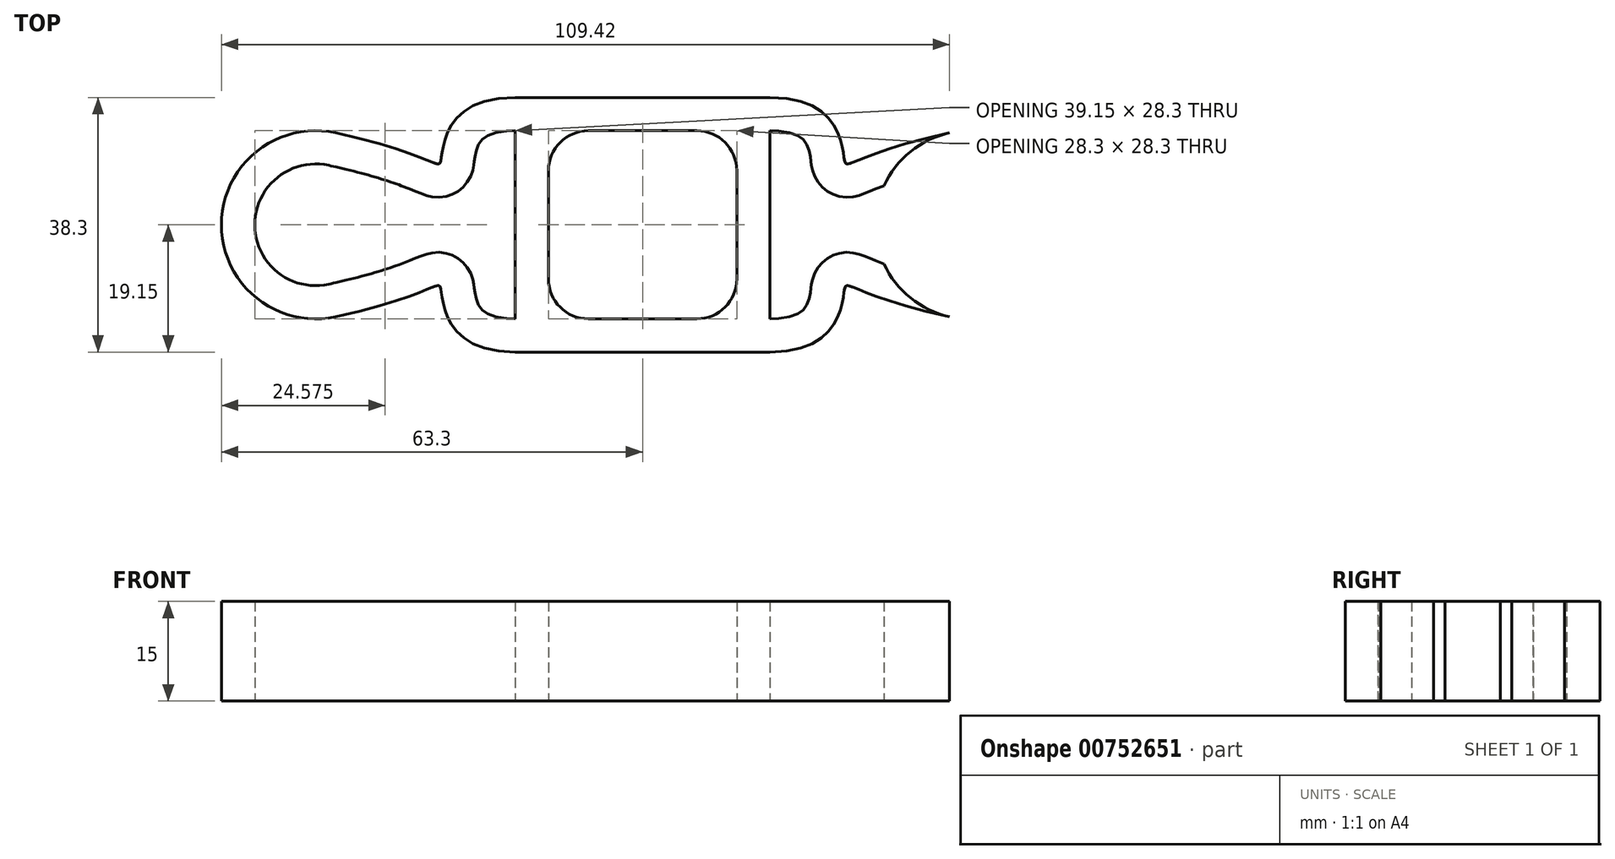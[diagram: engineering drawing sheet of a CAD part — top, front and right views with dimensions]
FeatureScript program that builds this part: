
annotation { "Feature Type Name" : "Feature", "Feature Type Description" : "" }
export const myFeature = defineFeature(function(context is Context, id is Id, definition is map)
    precondition{}
    {
        {
            var Q0;
            Q0=qCreatedBy(makeId("Top.planeOp"),FACE);
            var sketch = newSketch(context, id + "F0", { "sketchPlane" : qUnion([Q0])});
            skLineSegment(sketch, "E0.bottom", {"start": v(14.15, 14.15) * mm, "end": v(-14.15, 14.15) * mm});
            skLineSegment(sketch, "E0.top", {"start": v(14.15, -14.15) * mm, "end": v(-14.15, -14.15) * mm});
            skLineSegment(sketch, "E0.left", {"start": v(14.15, 14.15) * mm, "end": v(14.15, -14.15) * mm});
            skLineSegment(sketch, "E0.right", {"start": v(-14.15, 14.15) * mm, "end": v(-14.15, -14.15) * mm});
            skPoint(sketch, "E0.middle", {"position": v(0, 0) * mm});
            skLineSegment(sketch, "E1.0", {"start": v(-19.15, 19.15) * mm, "end": v(-19.15, -19.15) * mm});
            skLineSegment(sketch, "E1.1", {"start": v(19.15, 19.15) * mm, "end": v(-19.15, 19.15) * mm});
            skLineSegment(sketch, "E1.2", {"start": v(19.15, 19.15) * mm, "end": v(19.15, -19.15) * mm});
            skLineSegment(sketch, "E1.3", {"start": v(19.15, -19.15) * mm, "end": v(-19.15, -19.15) * mm});
            skCircle(sketch, "E2", {"center": v(-49.15, 0) * mm, "radius": 14.15 * mm});
            skFitSpline(sketch, "E3", {"points": [v(-46.12, 13.82) * mm, v(-30.27, 10.06) * mm, v(-19.15, 19.15) * mm], "startDerivative": vector(90.17, -19.78) * mm, "endDerivative": vector(63.13, 0) * mm});
            skFitSpline(sketch, "E4.MirrorCS", {"points": [v(-46.12, -13.82) * mm, v(-30.27, -10.06) * mm, v(-19.15, -19.15) * mm], "startDerivative": vector(90.17, 19.78) * mm, "endDerivative": vector(63.13, 0) * mm});
            skFitSpline(sketch, "E5.MirrorCS", {"points": [v(46.12, 13.82) * mm, v(30.27, 10.06) * mm, v(19.15, 19.15) * mm], "startDerivative": vector(-90.17, -19.78) * mm, "endDerivative": vector(-63.13, 0) * mm});
            skCircle(sketch, "E6.MirrorC", {"center": v(49.15, 0) * mm, "radius": 14.15 * mm});
            skFitSpline(sketch, "E7.MirrorCS", {"points": [v(46.12, -13.82) * mm, v(30.27, -10.06) * mm, v(19.15, -19.15) * mm], "startDerivative": vector(-90.17, 19.78) * mm, "endDerivative": vector(-63.13, 0) * mm});
            skCircle(sketch, "E8.0", {"center": v(-49.15, 0) * mm, "radius": 9.15 * mm});
            skCircle(sketch, "E9.0", {"center": v(49.15, 0) * mm, "radius": 9.15 * mm});
            skFitSpline(sketch, "E10.0", {"points": [v(-47.19, 8.94) * mm, v(-46.28, 8.74) * mm, v(-44.59, 8.35) * mm, v(-42.37, 7.78) * mm, v(-40.46, 7.25) * mm, v(-38.82, 6.75) * mm, v(-37.44, 6.3) * mm, v(-36.3, 5.88) * mm, v(-35.5, 5.58) * mm, v(-34.96, 5.36) * mm, v(-34.59, 5.2) * mm, v(-34.24, 5.07) * mm, v(-33.92, 4.93) * mm, v(-33.6, 4.8) * mm, v(-33.27, 4.67) * mm, v(-32.98, 4.56) * mm, v(-32.7, 4.47) * mm, v(-32.47, 4.4) * mm, v(-32.21, 4.33) * mm, v(-31.9, 4.26) * mm, v(-31.54, 4.2) * mm, v(-31.1, 4.15) * mm, v(-30.59, 4.14) * mm, v(-30.08, 4.18) * mm, v(-29.62, 4.26) * mm, v(-29.27, 4.35) * mm, v(-28.9, 4.47) * mm, v(-28.52, 4.62) * mm, v(-28.16, 4.8) * mm, v(-27.8, 5.02) * mm, v(-27.46, 5.26) * mm, v(-27.15, 5.52) * mm, v(-26.88, 5.8) * mm, v(-26.63, 6.07) * mm, v(-26.42, 6.34) * mm, v(-26.18, 6.7) * mm, v(-25.95, 7.1) * mm, v(-25.76, 7.54) * mm, v(-25.63, 7.9) * mm, v(-25.54, 8.21) * mm, v(-25.47, 8.48) * mm, v(-25.43, 8.7) * mm, v(-25.39, 8.9) * mm, v(-25.36, 9.07) * mm, v(-25.34, 9.22) * mm, v(-25.32, 9.36) * mm, v(-25.3, 9.49) * mm, v(-25.28, 9.65) * mm, v(-25.25, 9.85) * mm, v(-25.22, 10.08) * mm, v(-25.18, 10.3) * mm, v(-25.13, 10.6) * mm, v(-25.05, 10.96) * mm, v(-24.94, 11.38) * mm, v(-24.8, 11.76) * mm, v(-24.63, 12.11) * mm, v(-24.44, 12.42) * mm, v(-24.23, 12.7) * mm, v(-23.97, 12.95) * mm, v(-23.64, 13.2) * mm, v(-23.18, 13.46) * mm, v(-22.55, 13.71) * mm, v(-21.7, 13.94) * mm, v(-20.6, 14.1) * mm, v(-19.66, 14.15) * mm, v(-19.15, 14.15) * mm]});
            skFitSpline(sketch, "E11.0", {"points": [v(-47.19, -8.94) * mm, v(-46.28, -8.74) * mm, v(-44.59, -8.35) * mm, v(-42.37, -7.78) * mm, v(-40.46, -7.25) * mm, v(-38.82, -6.75) * mm, v(-37.44, -6.3) * mm, v(-36.3, -5.88) * mm, v(-35.5, -5.58) * mm, v(-34.96, -5.36) * mm, v(-34.59, -5.2) * mm, v(-34.24, -5.07) * mm, v(-33.92, -4.93) * mm, v(-33.6, -4.8) * mm, v(-33.27, -4.67) * mm, v(-32.98, -4.56) * mm, v(-32.7, -4.47) * mm, v(-32.47, -4.4) * mm, v(-32.21, -4.33) * mm, v(-31.9, -4.26) * mm, v(-31.54, -4.2) * mm, v(-31.1, -4.15) * mm, v(-30.59, -4.14) * mm, v(-30.08, -4.18) * mm, v(-29.62, -4.26) * mm, v(-29.27, -4.35) * mm, v(-28.9, -4.47) * mm, v(-28.52, -4.62) * mm, v(-28.16, -4.8) * mm, v(-27.8, -5.02) * mm, v(-27.46, -5.26) * mm, v(-27.15, -5.52) * mm, v(-26.88, -5.8) * mm, v(-26.63, -6.07) * mm, v(-26.42, -6.34) * mm, v(-26.18, -6.7) * mm, v(-25.95, -7.1) * mm, v(-25.76, -7.54) * mm, v(-25.63, -7.9) * mm, v(-25.54, -8.21) * mm, v(-25.47, -8.48) * mm, v(-25.43, -8.7) * mm, v(-25.39, -8.9) * mm, v(-25.36, -9.07) * mm, v(-25.34, -9.22) * mm, v(-25.32, -9.36) * mm, v(-25.3, -9.49) * mm, v(-25.28, -9.65) * mm, v(-25.25, -9.85) * mm, v(-25.22, -10.08) * mm, v(-25.18, -10.3) * mm, v(-25.13, -10.6) * mm, v(-25.05, -10.96) * mm, v(-24.94, -11.38) * mm, v(-24.8, -11.76) * mm, v(-24.63, -12.11) * mm, v(-24.44, -12.42) * mm, v(-24.23, -12.7) * mm, v(-23.97, -12.95) * mm, v(-23.64, -13.2) * mm, v(-23.18, -13.46) * mm, v(-22.55, -13.71) * mm, v(-21.7, -13.94) * mm, v(-20.6, -14.1) * mm, v(-19.66, -14.15) * mm, v(-19.15, -14.15) * mm]});
            skFitSpline(sketch, "E12.0", {"points": [v(47.19, 8.94) * mm, v(46.28, 8.74) * mm, v(44.59, 8.35) * mm, v(42.37, 7.78) * mm, v(40.46, 7.25) * mm, v(38.82, 6.75) * mm, v(37.44, 6.3) * mm, v(36.3, 5.88) * mm, v(35.5, 5.58) * mm, v(34.96, 5.36) * mm, v(34.59, 5.2) * mm, v(34.24, 5.07) * mm, v(33.92, 4.93) * mm, v(33.6, 4.8) * mm, v(33.27, 4.67) * mm, v(32.98, 4.56) * mm, v(32.7, 4.47) * mm, v(32.47, 4.4) * mm, v(32.21, 4.33) * mm, v(31.9, 4.26) * mm, v(31.54, 4.2) * mm, v(31.1, 4.15) * mm, v(30.59, 4.14) * mm, v(30.08, 4.18) * mm, v(29.62, 4.26) * mm, v(29.27, 4.35) * mm, v(28.9, 4.47) * mm, v(28.52, 4.62) * mm, v(28.16, 4.8) * mm, v(27.8, 5.02) * mm, v(27.46, 5.26) * mm, v(27.15, 5.52) * mm, v(26.88, 5.8) * mm, v(26.63, 6.07) * mm, v(26.42, 6.34) * mm, v(26.18, 6.7) * mm, v(25.95, 7.1) * mm, v(25.76, 7.54) * mm, v(25.63, 7.9) * mm, v(25.54, 8.21) * mm, v(25.47, 8.48) * mm, v(25.43, 8.7) * mm, v(25.39, 8.9) * mm, v(25.36, 9.07) * mm, v(25.34, 9.22) * mm, v(25.32, 9.36) * mm, v(25.3, 9.49) * mm, v(25.28, 9.65) * mm, v(25.25, 9.85) * mm, v(25.22, 10.08) * mm, v(25.18, 10.3) * mm, v(25.13, 10.6) * mm, v(25.05, 10.96) * mm, v(24.94, 11.38) * mm, v(24.8, 11.76) * mm, v(24.63, 12.11) * mm, v(24.44, 12.42) * mm, v(24.23, 12.7) * mm, v(23.97, 12.95) * mm, v(23.64, 13.2) * mm, v(23.18, 13.46) * mm, v(22.55, 13.71) * mm, v(21.7, 13.94) * mm, v(20.6, 14.1) * mm, v(19.66, 14.15) * mm, v(19.15, 14.15) * mm]});
            skFitSpline(sketch, "E13.0", {"points": [v(47.19, -8.94) * mm, v(46.28, -8.74) * mm, v(44.59, -8.35) * mm, v(42.37, -7.78) * mm, v(40.46, -7.25) * mm, v(38.82, -6.75) * mm, v(37.44, -6.3) * mm, v(36.3, -5.88) * mm, v(35.5, -5.58) * mm, v(34.96, -5.36) * mm, v(34.59, -5.2) * mm, v(34.24, -5.07) * mm, v(33.92, -4.93) * mm, v(33.6, -4.8) * mm, v(33.27, -4.67) * mm, v(32.98, -4.56) * mm, v(32.7, -4.47) * mm, v(32.47, -4.4) * mm, v(32.21, -4.33) * mm, v(31.9, -4.26) * mm, v(31.54, -4.2) * mm, v(31.1, -4.15) * mm, v(30.59, -4.14) * mm, v(30.08, -4.18) * mm, v(29.62, -4.26) * mm, v(29.27, -4.35) * mm, v(28.9, -4.47) * mm, v(28.52, -4.62) * mm, v(28.16, -4.8) * mm, v(27.8, -5.02) * mm, v(27.46, -5.26) * mm, v(27.15, -5.52) * mm, v(26.88, -5.8) * mm, v(26.63, -6.07) * mm, v(26.42, -6.34) * mm, v(26.18, -6.7) * mm, v(25.95, -7.1) * mm, v(25.76, -7.54) * mm, v(25.63, -7.9) * mm, v(25.54, -8.21) * mm, v(25.47, -8.48) * mm, v(25.43, -8.7) * mm, v(25.39, -8.9) * mm, v(25.36, -9.07) * mm, v(25.34, -9.22) * mm, v(25.32, -9.36) * mm, v(25.3, -9.49) * mm, v(25.28, -9.65) * mm, v(25.25, -9.85) * mm, v(25.22, -10.08) * mm, v(25.18, -10.3) * mm, v(25.13, -10.6) * mm, v(25.05, -10.96) * mm, v(24.94, -11.38) * mm, v(24.8, -11.76) * mm, v(24.63, -12.11) * mm, v(24.44, -12.42) * mm, v(24.23, -12.7) * mm, v(23.97, -12.95) * mm, v(23.64, -13.2) * mm, v(23.18, -13.46) * mm, v(22.55, -13.71) * mm, v(21.7, -13.94) * mm, v(20.6, -14.1) * mm, v(19.66, -14.15) * mm, v(19.15, -14.15) * mm]});
            skSolve(sketch);
        }
        {
            var Q0;
            {var subQ0=sQuery(id+"F0.wireOp",EDGE,"E3");Q0=makeQuery(id+"F0.imprint","IMPRINT",FACE,{"disambiguationData":[TD([[makeQuery(id+"F0.imprint","IMPRINT",EDGE,{"derivedFrom":subQ0}),-1.0]])]});}
            var Q1;
            {var subQ5=sQuery(id+"F0.wireOp",EDGE,"E2");var subQ6=makeQuery(id+"F0.imprint","INTERSECT",VERTEX,{"derivedFrom":[subQ5,sQuery(id+"F0.wireOp",EDGE,"E3")]});Q1=makeQuery(id+"F0.imprint","IMPRINT",FACE,{"disambiguationData":[TD([[makeQuery(id+"F0.imprint","IMPRINT",EDGE,{"disambiguationData":[TD([[subQ6,1.0]])],"derivedFrom":subQ5}),1.0]])]});}
            var Q2;
            {var subQ0=sQuery(id+"F0.wireOp",EDGE,"E4.MirrorCS");Q2=makeQuery(id+"F0.imprint","IMPRINT",FACE,{"disambiguationData":[TD([[makeQuery(id+"F0.imprint","IMPRINT",EDGE,{"derivedFrom":subQ0}),1.0]])]});}
            var Q3;
            {var subQ0=sQuery(id+"F0.wireOp",EDGE,"E5.MirrorCS");Q3=makeQuery(id+"F0.imprint","IMPRINT",FACE,{"disambiguationData":[TD([[makeQuery(id+"F0.imprint","IMPRINT",EDGE,{"derivedFrom":subQ0}),1.0]])]});}
            var Q4;
            {var subQ5=sQuery(id+"F0.wireOp",EDGE,"E6.MirrorC");var subQ9=makeQuery(id+"F0.imprint","INTERSECT",VERTEX,{"derivedFrom":[sQuery(id+"F0.wireOp",EDGE,"E5.MirrorCS"),subQ5]});Q4=makeQuery(id+"F0.imprint","IMPRINT",FACE,{"disambiguationData":[TD([[makeQuery(id+"F0.imprint","IMPRINT",EDGE,{"disambiguationData":[TD([[subQ9,1.0]])],"derivedFrom":subQ5}),-1.0]])]});}
            var Q5;
            {var subQ0=sQuery(id+"F0.wireOp",EDGE,"E7.MirrorCS");Q5=makeQuery(id+"F0.imprint","IMPRINT",FACE,{"disambiguationData":[TD([[makeQuery(id+"F0.imprint","IMPRINT",EDGE,{"derivedFrom":subQ0}),-1.0]])]});}
            var Q6;
            Q6=makeQuery(id+"F0.imprint","IMPRINT",FACE,{"disambiguationData":[TD([[makeQuery(id+"F0.imprint","IMPRINT",EDGE,{"derivedFrom":sQuery(id+"F0.wireOp",EDGE,"E0.bottom")}),-1.0]])]});
            extrude(context, id + "F1", {"entities" : qUnion([Q0, Q1, Q2, Q3, Q4, Q5, Q6]), "depth" : 15 * mm, "offsetDistance" : 25 * mm});
        }
        {
            var Q0;
            Q0=makeQuery(id+"F1.opExtrude","SWEPT_EDGE",EDGE,{"disambiguationData":[OSD([sQuery(id+"F0.wireOp",EDGE,"E0.bottom"),sQuery(id+"F0.wireOp",EDGE,"E0.right")])]});
            var Q1;
            Q1=makeQuery(id+"F1.opExtrude","SWEPT_EDGE",EDGE,{"disambiguationData":[OSD([sQuery(id+"F0.wireOp",EDGE,"E0.bottom"),sQuery(id+"F0.wireOp",EDGE,"E0.left")])]});
            var Q2;
            Q2=makeQuery(id+"F1.opExtrude","SWEPT_EDGE",EDGE,{"disambiguationData":[OSD([sQuery(id+"F0.wireOp",EDGE,"E0.top"),sQuery(id+"F0.wireOp",EDGE,"E0.left")])]});
            var Q3;
            Q3=makeQuery(id+"F1.opExtrude","SWEPT_EDGE",EDGE,{"disambiguationData":[OSD([sQuery(id+"F0.wireOp",EDGE,"E0.top"),sQuery(id+"F0.wireOp",EDGE,"E0.right")])]});
            fillet(context, id + "F2", {"entities" : qUnion([Q0, Q1, Q2, Q3]), "radius" : 6 * mm, "tangentPropagation" : true, "allowEdgeOverflow" : false});
        }
    });
